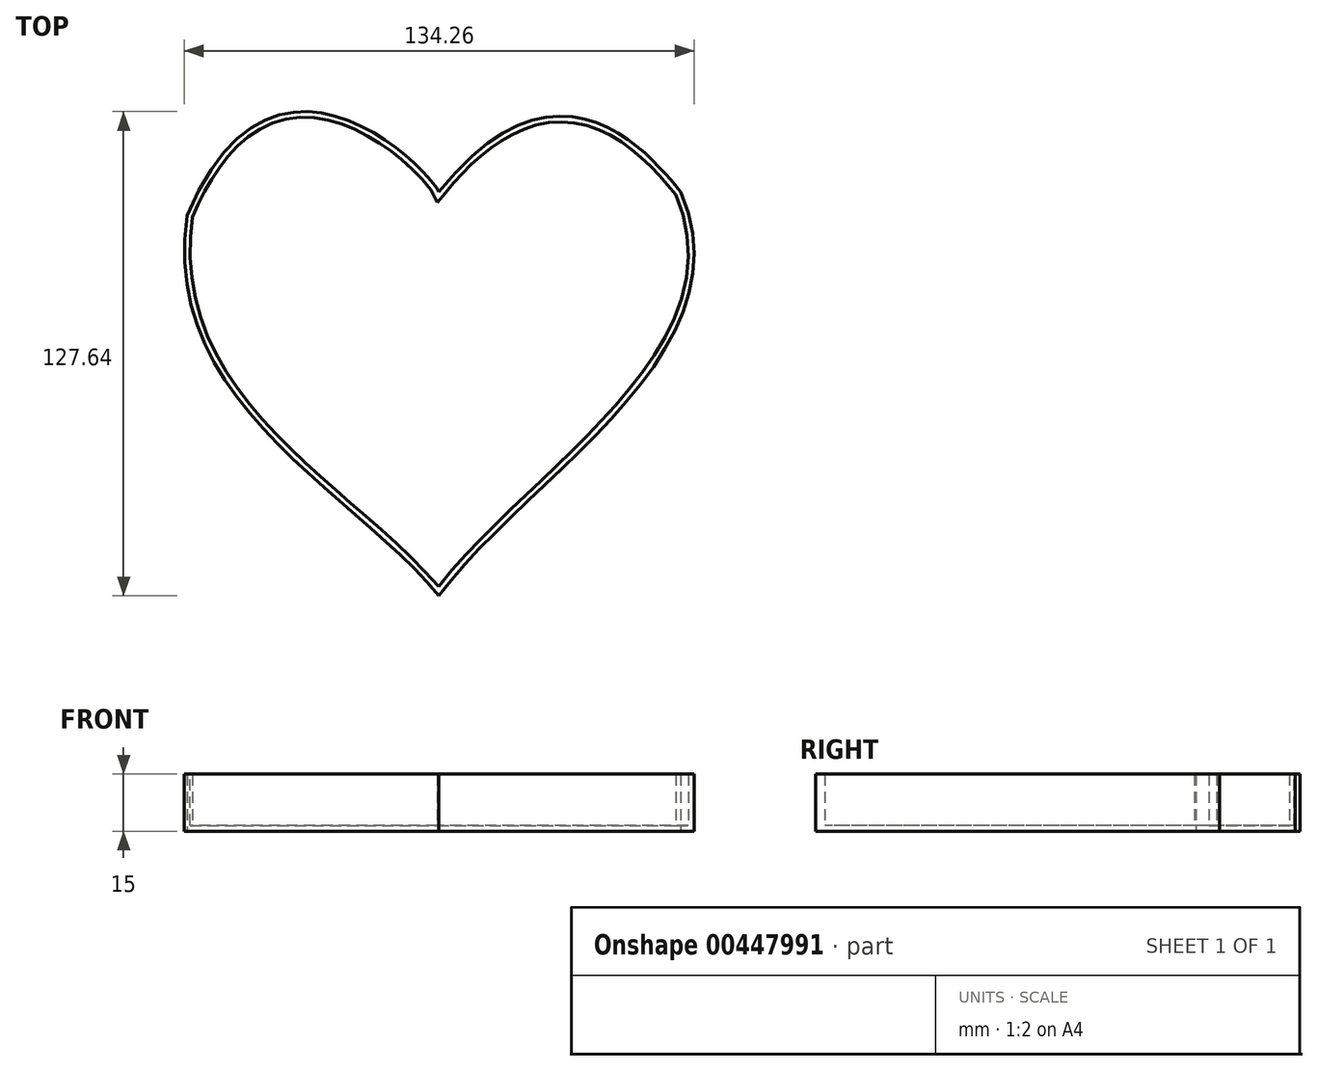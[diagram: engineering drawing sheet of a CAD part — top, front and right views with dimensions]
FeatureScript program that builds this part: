
annotation { "Feature Type Name" : "Feature", "Feature Type Description" : "" }
export const myFeature = defineFeature(function(context is Context, id is Id, definition is map)
    precondition{}
    {
        {
            var Q0;
            Q0=qCreatedBy(makeId("Top.planeOp"),FACE);
            var sketch = newSketch(context, id + "F0", { "sketchPlane" : qUnion([Q0])});
            skFitSpline(sketch, "E0", {"points": [v(0, 61.69) * mm, v(63.79, 61.69) * mm], "startDerivative": vector(102.38, 127.58) * mm, "endDerivative": vector(13.38, -13.38) * mm});
            skFitSpline(sketch, "E1", {"points": [v(63.79, 61.69) * mm, v(0, -44.82) * mm], "startDerivative": vector(54.65, -129.72) * mm, "endDerivative": vector(-69.97, -95.26) * mm});
            skFitSpline(sketch, "E2", {"points": [v(-66.36, 55.42) * mm, v(0, -44.82) * mm], "startDerivative": vector(-20.94, -148.95) * mm, "endDerivative": vector(68.29, -84.3) * mm});
            skFitSpline(sketch, "E3", {"points": [v(0, 61.69) * mm, v(-66.36, 55.42) * mm], "startDerivative": vector(-7.44, 16.93) * mm, "endDerivative": vector(-68.73, -163.36) * mm});
            skSolve(sketch);
        }
        {
            var Q0;
            Q0=makeQuery(id+"F0.imprint","IMPRINT",FACE,{"disambiguationData":[TD([[makeQuery(id+"F0.imprint","IMPRINT",EDGE,{"derivedFrom":sQuery(id+"F0.wireOp",EDGE,"E0")}),-1.0]])]});
            extrude(context, id + "F1", {"entities" : qUnion([Q0]), "depth" : 15 * mm});
        }
        {
            var Q0;
            Q0=makeQuery(id+"F1.opExtrude","CAP_FACE",FACE,{"disambiguationData":[OSD([sQuery(id+"F0.wireOp",EDGE,"E0"),sQuery(id+"F0.wireOp",EDGE,"E1"),sQuery(id+"F0.wireOp",EDGE,"E2"),sQuery(id+"F0.wireOp",EDGE,"E3")])],"isStart":false});
            shell(context, id + "F2", {"entities" : qUnion([Q0]), "thickness" : 1.5 * mm});
        }
    });
